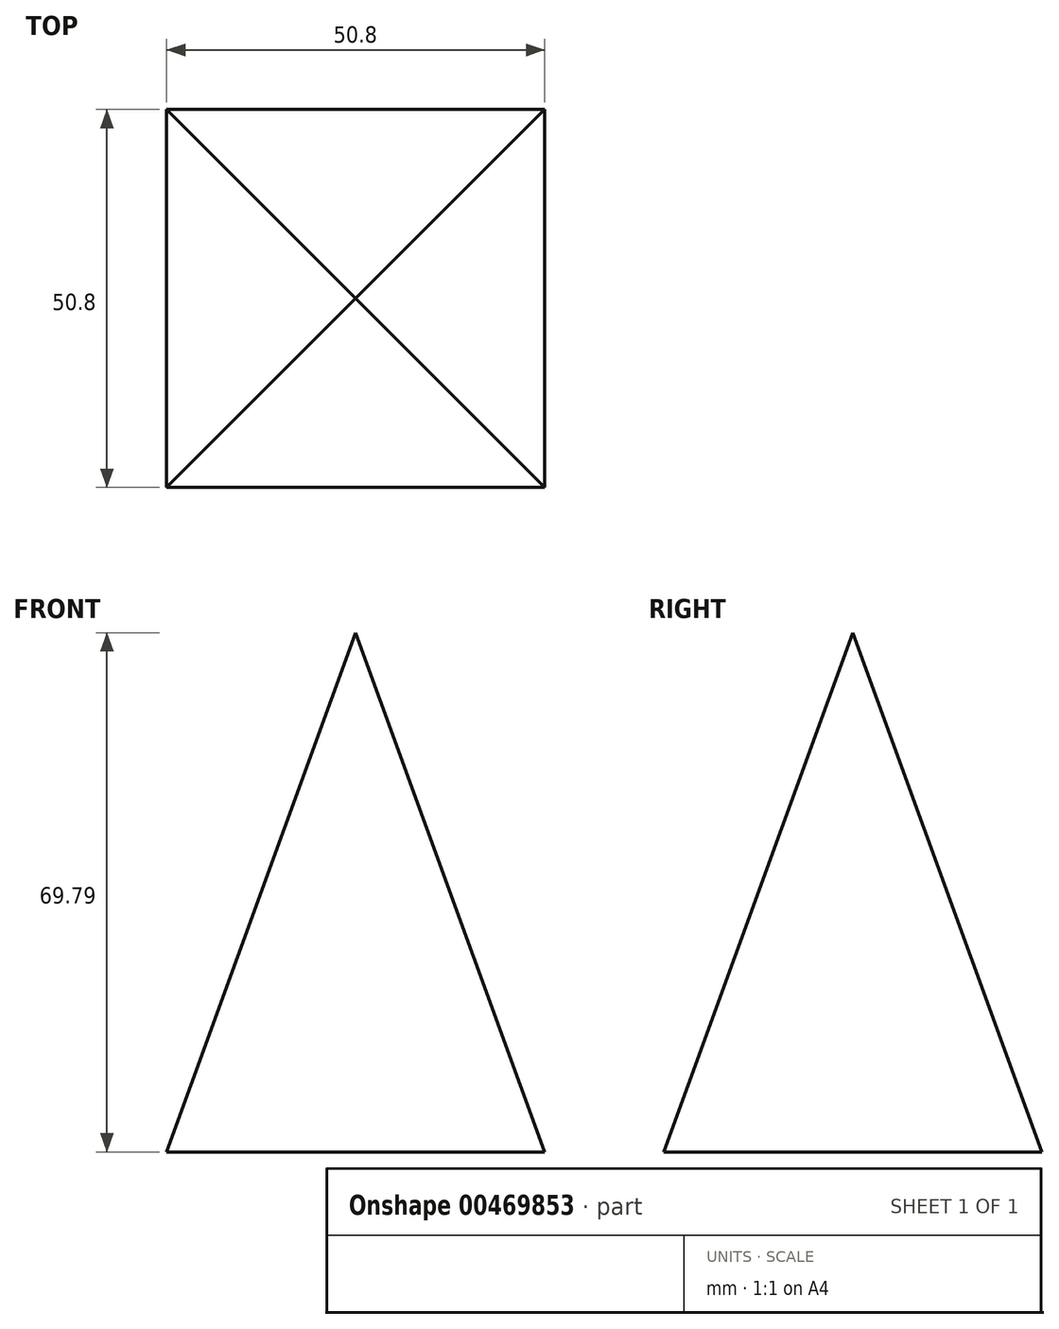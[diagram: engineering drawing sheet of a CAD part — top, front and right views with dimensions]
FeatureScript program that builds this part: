
annotation { "Feature Type Name" : "Feature", "Feature Type Description" : "" }
export const myFeature = defineFeature(function(context is Context, id is Id, definition is map)
    precondition{}
    {
        {
            var Q0;
            Q0=qCreatedBy(makeId("Top.planeOp"),FACE);
            var sketch = newSketch(context, id + "F0", { "sketchPlane" : qUnion([Q0])});
            skLineSegment(sketch, "E0.bottom", {"start": v(-25.4, 25.4) * mm, "end": v(25.4, 25.4) * mm});
            skLineSegment(sketch, "E0.top", {"start": v(-25.4, -25.4) * mm, "end": v(25.4, -25.4) * mm});
            skLineSegment(sketch, "E0.left", {"start": v(-25.4, 25.4) * mm, "end": v(-25.4, -25.4) * mm});
            skLineSegment(sketch, "E0.right", {"start": v(25.4, 25.4) * mm, "end": v(25.4, -25.4) * mm});
            skPoint(sketch, "E0.middle", {"position": v(0, 0) * mm});
            skSolve(sketch);
        }
        {
            var Q0;
            Q0=makeQuery(id+"F0.imprint","IMPRINT",FACE,{"disambiguationData":[TD([[makeQuery(id+"F0.imprint","IMPRINT",EDGE,{"derivedFrom":sQuery(id+"F0.wireOp",EDGE,"E0.bottom")}),-1.0]])]});
            extrude(context, id + "F1", {"entities" : qUnion([Q0]), "depth" : 101.6 * mm, "hasDraft" : true, "draftAngle" : 20 * degree, "draftPullDirection" : true});
        }
    });
